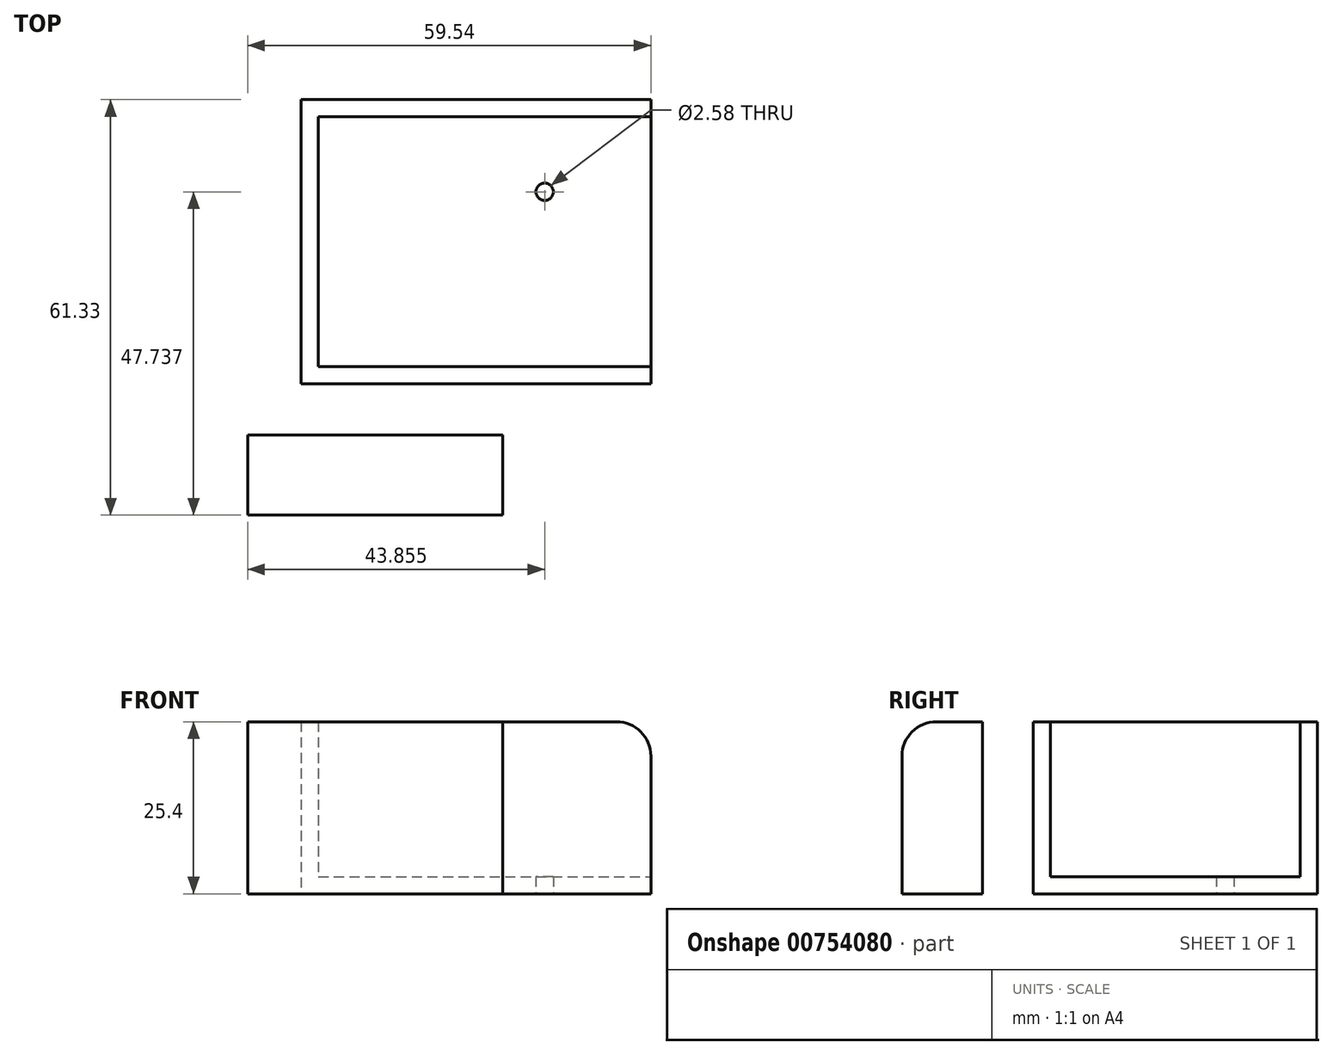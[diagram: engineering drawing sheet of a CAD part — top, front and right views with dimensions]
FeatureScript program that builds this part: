
annotation { "Feature Type Name" : "Feature", "Feature Type Description" : "" }
export const myFeature = defineFeature(function(context is Context, id is Id, definition is map)
    precondition{}
    {
        {
            var Q0;
            Q0=qCreatedBy(makeId("Top.planeOp"),FACE);
            var sketch = newSketch(context, id + "F0", { "sketchPlane" : qUnion([Q0])});
            skLineSegment(sketch, "E0.bottom", {"start": v(-11.74, -41.94) * mm, "end": v(39.91, -41.94) * mm});
            skLineSegment(sketch, "E0.top", {"start": v(-11.74, 0) * mm, "end": v(39.91, 0) * mm});
            skLineSegment(sketch, "E0.left", {"start": v(-11.74, -41.94) * mm, "end": v(-11.74, 0) * mm});
            skLineSegment(sketch, "E0.right", {"start": v(39.91, -41.94) * mm, "end": v(39.91, 0) * mm});
            skLineSegment(sketch, "E1.bottom", {"start": v(18.05, -49.47) * mm, "end": v(-19.63, -49.47) * mm});
            skLineSegment(sketch, "E1.top", {"start": v(18.05, -61.33) * mm, "end": v(-19.63, -61.33) * mm});
            skLineSegment(sketch, "E1.left", {"start": v(18.05, -49.47) * mm, "end": v(18.05, -61.33) * mm});
            skLineSegment(sketch, "E1.right", {"start": v(-19.63, -49.47) * mm, "end": v(-19.63, -61.33) * mm});
            skSolve(sketch);
        }
        {
            var Q0;
            Q0=makeQuery(id+"F0.imprint","IMPRINT",FACE,{"disambiguationData":[TD([[makeQuery(id+"F0.imprint","IMPRINT",EDGE,{"derivedFrom":sQuery(id+"F0.wireOp",EDGE,"E0.bottom")}),1.0]])]});
            var Q1;
            Q1=makeQuery(id+"F0.imprint","IMPRINT",FACE,{"disambiguationData":[TD([[makeQuery(id+"F0.imprint","IMPRINT",EDGE,{"derivedFrom":sQuery(id+"F0.wireOp",EDGE,"E1.bottom")}),1.0]])]});
            extrude(context, id + "F1", {"entities" : qUnion([Q0, Q1]), "depth" : 25.4 * mm, "offsetDistance" : 25.4 * mm});
        }
        {
            var Q0;
            Q0=makeQuery(id+"F1.opExtrude","CAP_EDGE",EDGE,{"disambiguationData":[OSD([sQuery(id+"F0.wireOp",EDGE,"E1.top")])],"isStart":false});
            var Q1;
            Q1=makeQuery(id+"F1.opExtrude","CAP_EDGE",EDGE,{"disambiguationData":[OSD([sQuery(id+"F0.wireOp",EDGE,"E0.right")])],"isStart":false});
            fillet(context, id + "F2", {"entities" : qUnion([Q0, Q1]), "radius" : 5.08 * mm, "tangentPropagation" : true, "allowEdgeOverflow" : false});
        }
        {
            var Q0;
            Q0=makeQuery(id+"F1.opExtrude","CAP_FACE",FACE,{"disambiguationData":[OSD([sQuery(id+"F0.wireOp",EDGE,"E0.bottom"),sQuery(id+"F0.wireOp",EDGE,"E0.top"),sQuery(id+"F0.wireOp",EDGE,"E0.left"),sQuery(id+"F0.wireOp",EDGE,"E0.right")])],"isStart":false});
            var Q1;
            Q1=makeQuery(id+"F2.opFillet","BLEND_FACE",FACE,{"disambiguationData":[OSD([sQuery(id+"F0.wireOp",EDGE,"E0.right")])]});
            var Q2;
            Q2=makeQuery(id+"F1.opExtrude","SWEPT_FACE",FACE,{"disambiguationData":[OSD([sQuery(id+"F0.wireOp",EDGE,"E0.right")])]});
            shell(context, id + "F3", {"entities" : qUnion([Q0, Q1, Q2]), "thickness" : 2.54 * mm});
        }
        {
            var Q0;
            Q0=qCreatedBy(makeId("Top.planeOp"),FACE);
            var sketch = newSketch(context, id + "F4", { "sketchPlane" : qUnion([Q0])});
            skCircle(sketch, "E2", {"center": v(24.23, -13.6) * mm, "radius": 7.75 * mm});
            skSolve(sketch);
        }
        {
            var Q0;
            Q0=sQuery(id+"F4.wireOp",VERTEX,"E2.center");
            var Q1;
            Q1=makeQuery(id+"F1.opExtrude","SWEPT_BODY",BODY,{"disambiguationData":[OSD([sQuery(id+"F0.wireOp",EDGE,"E0.bottom"),sQuery(id+"F0.wireOp",EDGE,"E0.top"),sQuery(id+"F0.wireOp",EDGE,"E0.left"),sQuery(id+"F0.wireOp",EDGE,"E0.right")])]});
            hole(context, id + "F5", {"style" : HoleStyle.SIMPLE, "endStyle" : HoleEndStyle.THROUGH, "oppositeDirection" : true, "standardTappedOrClearance" : lookupTablePath({ "standard" : "ANSI", "engagement" : "75%", "pitch" : "40 tpi", "size" : "#5", "type" : "Tapped" }), "standardBlindInLast" : lookupTablePath({ "standard" : "ANSI", "engagement" : "75%", "pitch" : "40 tpi", "size" : "#5", "type" : "Tapped" }), "holeDiameter" : 2.58 * mm, "majorDiameter" : 3.17 * mm, "showTappedDepth" : true, "isTappedThrough" : true, "tappedDepth" : 12.7 * mm, "tapClearance" : 3, "locations" : qUnion([Q0]), "scope" : qUnion([Q1])});
        }
    });
